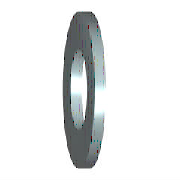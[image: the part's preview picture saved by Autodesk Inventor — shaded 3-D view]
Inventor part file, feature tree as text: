
AUTODESK INVENTOR PART (.ipt)
format: ipt  version: 2022 (Build 260153000, 153)  size: 109,568 bytes
history: native  units: mm (DEFAULTED — no unit token found)
features: other x1, plane x1, sketch x1
ambient origin geometry x7: Origin, YZ Plane, XY Plane, X Axis, Y Axis, Z Axis, Center Point
bodies: Solid1 (feature_tree), Body (feature_tree)
feature tree (3):
  other  "Work Axis1"
  plane  "Work Plane1"
  sketch  "Sketch"  dims[d0=3.2mm d1=9.0mm d2=0.8mm d3=0.0mm d4=0.0mm d5=0.0mm d6=0.0mm d7=0.0mm]
